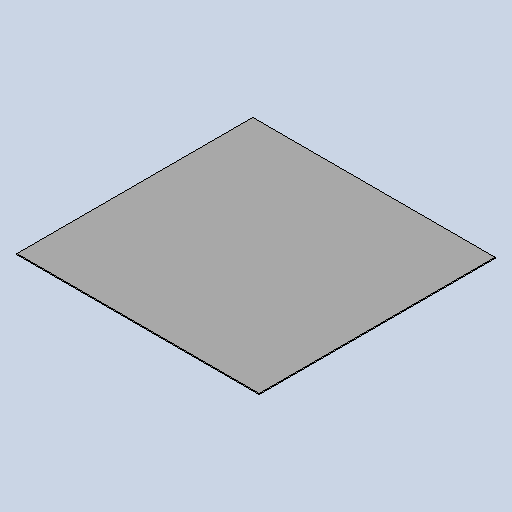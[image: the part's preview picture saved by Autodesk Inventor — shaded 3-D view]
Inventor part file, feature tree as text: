
AUTODESK INVENTOR PART (.ipt)
format: ipt  version: 2025.3 (Build 293356030, 356C)  size: 139,776 bytes
history: native  units: mm
features: other x2, sheet_metal_op x1, sketch x1
ambient origin geometry x8: Origin, YZ Plane, XZ Plane, XY Plane, X Axis, Y Axis, Z Axis, Center Point
bodies: Solid1 (feature_tree)
feature tree (4):
  sheet_metal_op  "Face1"
  sketch  "Sketch1"  dims[d2=493.0mm d3=2.0mm d18=480.0mm]
  other  "Plate1"
  other  "Definition1"
